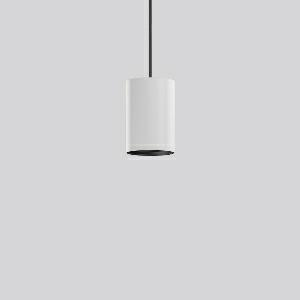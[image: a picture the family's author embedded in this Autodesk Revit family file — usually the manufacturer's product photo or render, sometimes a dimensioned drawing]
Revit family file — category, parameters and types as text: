
# Revit family: deecos_p_maxi_911530_002_2_76_6710
name_source: partatom
category: Lighting Fixtures
units: mm (PartAtom-declared; Revit-internal decimal feet)

## family parameters
Cut with Voids When Loaded = No
Host = Face
Light Source = No
Part Type = Normal
Room Calculation Point = No
Round Connector Dimension = Use Diameter
Shared = No

## types (1)
- DEECOS P maxi (1 x LED Modul 927, 3150 lm, 2700)
    Apparent Load = 25 VA
    Approval mark = CE
    CIE Flux Codes = 100 100 100 100 100
    Color Rendering = 92
    Color Temperature = 2700
    Default Elevation = 1800 mm
    Description = Series: DEECOS P maxi
Cylindrical pendant luminaire. Housing: die-cast aluminium, powder-coated. Canopy made of powder-coated sheet steel with magnetic attachment. Optical assembly with reflector made of MIRO-Silver with 98% total light reflection for outstanding efficiency - can be changed without tools. Best colour rendering index Ra>90. Transparent suspension cable 2 m, can be shortened. High quality converter without flickering and stroboscopic effect. The following accessories can be mounted without use of tools: interchangeable lenses, honeycomb louvre, clear and frosted diffusers, white interchangeable plastic ring. Decorative recessed suspension set available as accessory. 
Colour: traffic white, matt (RAL 9016)
Diameter: 123 mm
Height: 181 mm
Suspension length: 2000 mm
Lamp: LED
Socket: without socket
Colour temperature: 2700K
Colour rendering index (CRI): 92
System power: 25 W
Rated luminous flux: 3150 lm
Luminous efficiency: 126 lm/W
Control gear: Converter, dimmable, DALI
Protection class: I
Type of protection: IP 20
    Height = 181 mm
    Lamp = 1 x LED Modul 927
    Lamp Light Flux = 3150 lm
    Lamp count = 1
    Length = 123 mm
    Lifetime = 50000 h
    Luminous efficacy = 126 lm/W
    Manufacturer = RZB
    ModVariant = No
    Model = 911530.002.2.76
    Mounting Place = Ceiling
    Mounting Type = Pendant
    Number of Poles = 1
    OnlyDefault = Yes
    Power Factor = 1
    Product Name = DEECOS P maxi
    Product group = Pendant luminaires
    ProductGroupID = 902
    Protection Class = Protection class I
    Protection Degree = IP 20
    RLX_Detail_Level = 1
    RLX_Emergency_Light_Flux = 0 lm
    RLX_Emergency_Type = 0
    RLX_Emergency_Type_DB = No
    RlxData = <blob elided: 35533 chars, md5=75aae09b>
    Socket = socket
    Standby Power = 0 W
    System Light Flux = 3150 lm
    System Power = 25 W
    Type Comments = Product without accessories
    Type Image = 911480.002.jpg
    URL = http://relux.com
    VarID = ---
    Voltage = 230 V
    Voltage Range = 220-240 V
    Weight = 0.00 kg
    Width = 0 mm  [stored 0 ft]

note: [stored X ft] marks values corroborated as IEEE doubles in the binary element streams (Revit-internal decimal feet)

## geometry (parser evidence)
native form markers: Blend x4, Sweep x9
no freeform markers — native parametric forms only
